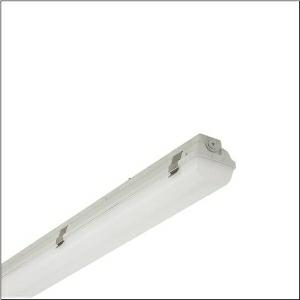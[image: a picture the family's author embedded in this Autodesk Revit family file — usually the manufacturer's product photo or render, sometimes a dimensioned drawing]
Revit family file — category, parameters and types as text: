
# Revit family: monsun_r__21_eco_51fj10dl45a_5ac6
name_source: partatom
category: Lighting Fixtures
units: mm (PartAtom-declared; Revit-internal decimal feet)

## family parameters
Cut with Voids When Loaded = No
Host = Face
Light Source = No
Part Type = Normal
Room Calculation Point = No
Round Connector Dimension = Use Diameter
Shared = No

## types (1)
- Monsun® 21 Eco (1 x LED, 5100 lm, 36 W, 4000K)
    Apparent Load = 36 VA
    CIE Flux Codes = 41 70 89 90 100
    Color Rendering = 80
    Color Temperature = 4000K
    Default Elevation = 1800 mm
    Description = Monsun® 21 Eco, damp-proof luminaire, primary optical cover: diffuser, of PMMA, frosted, light emission: direct distribution, primary light characteristic: symmetric, installation type: suspended mounting, surface-mounted, LED, rated luminous flux: 5.100lm, luminous efficacy: 142lm/W, light colour: 840, colour temperature: 4000K, control gear: DALI, with terminal, 5-pole, max. 2.5mm², mains connection: 220..240V, AC, 50/60Hz, rated input power: 36W, housing, of glass-fibre reinforced polyester, light grey (RAL 7035), length: 1.277mm, width: 90mm, height: 95mm, clip for enclosure, of spring steel V2A, protection rating (complete): IP66, insulation class (complete): insulation class I (protective earthing), certification: CE, UKCA, protection symbol: D, impact resistance: IK02, permissible operating ambient temperature: -20..+35°C, corresponds to IFS (International Featured Standards) requirements for safety and quality in the food industry, contact your sales advisor before using the luminaires in applications with unclear chemical exposure, large temperature fluctuations or condensation-forming humidity, packaging unit: 1 piece
    Height = 103 mm
    Lamp = 1 x LED
    Lamp Light Flux = 5100 lm
    Lamp Power = 36 W
    Lamp count = 1
    Length = 1277 mm
    Luminous efficacy = 142 lm/W
    Manufacturer = Siteco
    ModVariant = No
    Model = 51FJ10DL45A
    Mounting Place = Ceiling
    Mounting Type = Surface mounted
    Number of Poles = 1
    OnlyDefault = Yes
    Power Factor = 1
    Product Name = Monsun® 21 Eco
    Product group = damp-proof luminaire
    ProductGroupID = 300
    Protection Class = Protection class I
    Protection Degree = IP 66
    RLX_Detail_Level = 1
    RLX_Emergency_Light_Flux = 0 lm
    RLX_Emergency_Type = 0
    RLX_Emergency_Type_DB = No
    RlxData = <blob elided: 33445 chars, md5=5554190f>
    Socket = socket
    Standby Power = 0 W
    System Light Flux = 5100 lm
    System Power = 36 W
    Type Comments = Product without accessories
    Type Image = l_1007218.jpg
    URL = http://relux.com
    VarID = ---
    Voltage = 0 V
    Weight = 0.00 kg
    Width = 90 mm

## geometry (parser evidence)
native form markers: Blend x4, Sweep x12
no freeform markers — native parametric forms only
